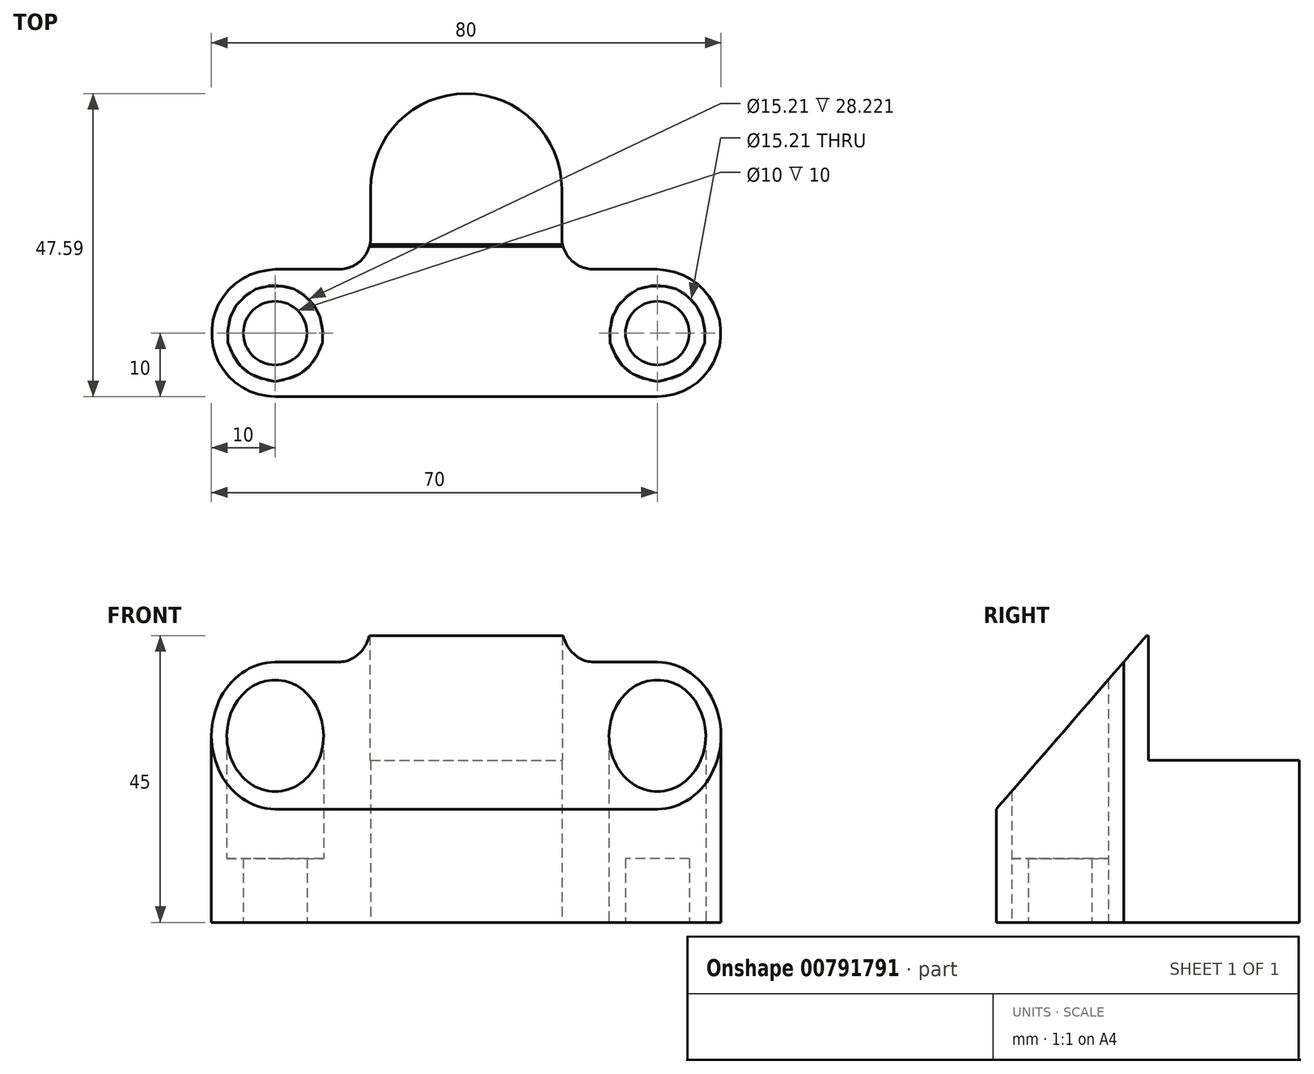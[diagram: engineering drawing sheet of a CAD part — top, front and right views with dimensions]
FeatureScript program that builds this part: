
annotation { "Feature Type Name" : "Feature", "Feature Type Description" : "" }
export const myFeature = defineFeature(function(context is Context, id is Id, definition is map)
    precondition{}
    {
        {
            var Q0;
            Q0=qCreatedBy(makeId("Top.planeOp"),FACE);
            var sketch = newSketch(context, id + "F0", { "sketchPlane" : qUnion([Q0])});
            skCircle(sketch, "E0", {"center": v(-30, 0) * mm, "radius": 5 * mm});
            skLineSegment(sketch, "E1", {"start": v(0, 0) * mm, "end": v(-30, 0) * mm, "construction": true});
            skArc(sketch, "E2.0.endCap", {"start": v(-30, -10) * mm, "mid": v(-40, 0) * mm, "end": v(-30, 10) * mm});
            skLineSegment(sketch, "E2.0.left", {"start": v(0, -10) * mm, "end": v(-30, -10) * mm});
            skLineSegment(sketch, "E2.0.right", {"start": v(-20, 10) * mm, "end": v(-30, 10) * mm});
            skLineSegment(sketch, "E3", {"start": v(0, 10) * mm, "end": v(0, -10) * mm});
            skLineSegment(sketch, "E4", {"start": v(0, 0) * mm, "end": v(0, 22.6) * mm, "construction": true});
            skArc(sketch, "E5.0.endCap", {"start": v(-15, 22.6) * mm, "mid": v(-10.6, 33.2) * mm, "end": v(0, 37.6) * mm});
            skLineSegment(sketch, "E5.0.left", {"start": v(-15, 15) * mm, "end": v(-15, 22.6) * mm});
            skLineSegment(sketch, "E6", {"start": v(0, 37.6) * mm, "end": v(0, -10) * mm});
            skArc(sketch, "E7.filletArc", {"start": v(-20, 10) * mm, "mid": v(-16.46, 11.46) * mm, "end": v(-15, 15) * mm});
            skLineSegment(sketch, "E8.MirrorCS", {"start": v(0, 0) * mm, "end": v(30, 0) * mm, "construction": true});
            skLineSegment(sketch, "E9.MirrorCS", {"start": v(15, 15) * mm, "end": v(15, 22.6) * mm});
            skArc(sketch, "E10.MirrorCS", {"start": v(15, 22.6) * mm, "mid": v(10.6, 33.2) * mm, "end": v(0, 37.6) * mm});
            skLineSegment(sketch, "E11.MirrorCS", {"start": v(20, 10) * mm, "end": v(30, 10) * mm});
            skLineSegment(sketch, "E12.MirrorCS", {"start": v(0, -10) * mm, "end": v(30, -10) * mm});
            skCircle(sketch, "E13.MirrorC", {"center": v(30, 0) * mm, "radius": 5 * mm});
            skArc(sketch, "E14.MirrorCS", {"start": v(20, 10) * mm, "mid": v(16.46, 11.46) * mm, "end": v(15, 15) * mm});
            skArc(sketch, "E15.MirrorCS", {"start": v(30, -10) * mm, "mid": v(40, 0) * mm, "end": v(30, 10) * mm});
            skCircle(sketch, "E16", {"center": v(-30, 0) * mm, "radius": 7.6 * mm});
            skCircle(sketch, "E17", {"center": v(30, 0) * mm, "radius": 7.6 * mm});
            skSolve(sketch);
        }
        {
            var Q0;
            Q0 = qSketchRegion(id + "F0", true);
            extrude(context, id + "F1", {"entities" : qUnion([Q0]), "depth" : 45 * mm, "offsetDistance" : 25 * mm});
        }
        {
            var Q0;
            Q0=qCreatedBy(makeId("Right.planeOp"),FACE);
            var sketch = newSketch(context, id + "F2", { "sketchPlane" : qUnion([Q0])});
            skLineSegment(sketch, "E18", {"start": v(-10.25, 17.48) * mm, "end": v(16.45, 48.31) * mm});
            skLineSegment(sketch, "E19", {"start": v(16.45, 48.31) * mm, "end": v(-20.42, 48.31) * mm});
            skLineSegment(sketch, "E20", {"start": v(-20.42, 48.31) * mm, "end": v(-10.25, 17.48) * mm});
            skSolve(sketch);
        }
        {
            var Q0;
            Q0 = qSketchRegion(id + "F2", true);
            extrude(context, id + "F3", {"entities" : qUnion([Q0]), "operationType" : NewBodyOperationType.REMOVE, "endBound" : BoundingType.THROUGH_ALL, "oppositeDirection" : true, "depth" : 25 * mm, "offsetDistance" : 25 * mm, "hasSecondDirection" : true, "secondDirectionBound" : BoundingType.THROUGH_ALL, "secondDirectionOppositeDirection" : false, "secondDirectionDepth" : 25 * mm});
        }
        {
            var Q0;
            Q0=qCreatedBy(makeId("Right.planeOp"),FACE);
            var sketch = newSketch(context, id + "F4", { "sketchPlane" : qUnion([Q0])});
            skLineSegment(sketch, "E21", {"start": v(13.9, 45.43) * mm, "end": v(13.9, 25.43) * mm});
            skLineSegment(sketch, "E22", {"start": v(13.9, 25.43) * mm, "end": v(42.83, 25.43) * mm});
            skLineSegment(sketch, "E23", {"start": v(42.83, 25.43) * mm, "end": v(42.83, 53.08) * mm});
            skLineSegment(sketch, "E24", {"start": v(42.83, 53.08) * mm, "end": v(13.9, 45.43) * mm});
            skSolve(sketch);
        }
        {
            var Q0;
            Q0 = qSketchRegion(id + "F4", true);
            extrude(context, id + "F5", {"entities" : qUnion([Q0]), "operationType" : NewBodyOperationType.REMOVE, "endBound" : BoundingType.THROUGH_ALL, "oppositeDirection" : true, "depth" : 25 * mm, "offsetDistance" : 25 * mm, "hasSecondDirection" : true, "secondDirectionBound" : BoundingType.THROUGH_ALL, "secondDirectionOppositeDirection" : false, "secondDirectionDepth" : 25 * mm});
        }
        {
            var Q0;
            Q0=makeQuery(id+"F0.imprint","IMPRINT",FACE,{"disambiguationData":[TD([[makeQuery(id+"F0.imprint","IMPRINT",EDGE,{"derivedFrom":sQuery(id+"F0.wireOp",EDGE,"E0")}),-1.0]])]});
            extrude(context, id + "F6", {"entities" : qUnion([Q0]), "operationType" : NewBodyOperationType.ADD, "depth" : 10 * mm, "offsetDistance" : 25 * mm});
        }
        {
            var Q0;
            Q0=makeQuery(id+"F0.imprint","IMPRINT",FACE,{"disambiguationData":[TD([[makeQuery(id+"F0.imprint","IMPRINT",EDGE,{"derivedFrom":sQuery(id+"F0.wireOp",EDGE,"E13.MirrorC")}),1.0]])]});
            extrude(context, id + "F7", {"entities" : qUnion([Q0]), "operationType" : NewBodyOperationType.ADD, "depth" : 10 * mm, "offsetDistance" : 25 * mm});
        }
    });
